annotation { "Feature Type Name" : "Feature", "Feature Type Description" : "" }
export const myFeature = defineFeature(function(context is Context, id is Id, definition is map)
    precondition{}
    {
        {
            var Q0;
            Q0=qCreatedBy(makeId("Top.planeOp"),FACE);
            var sketch = newSketch(context, id + "F0", { "sketchPlane" : qUnion([Q0])});
            skLineSegment(sketch, "E0.bottom", {"start": v(-26.5, -42.5) * mm, "end": v(26.5, -42.5) * mm});
            skLineSegment(sketch, "E0.top", {"start": v(-23.72, 42.5) * mm, "end": v(-23.1, 42.5) * mm});
            skLineSegment(sketch, "E0.left", {"start": v(-26.5, -42.5) * mm, "end": v(-26.5, 0) * mm});
            skLineSegment(sketch, "E0.right", {"start": v(26.5, -42.5) * mm, "end": v(26.5, 0) * mm});
            skPoint(sketch, "E0.middle", {"position": v(0, 0) * mm});
            skLineSegment(sketch, "E1.top", {"start": v(-0.6, 85) * mm, "end": v(0.6, 85) * mm});
            skLineSegment(sketch, "E1.left", {"start": v(-0.6, 0) * mm, "end": v(-0.6, 41.9) * mm});
            skLineSegment(sketch, "E1.right", {"start": v(0.6, 0) * mm, "end": v(0.6, 41.9) * mm});
            skPoint(sketch, "E1.middle", {"position": v(0, 42.5) * mm});
            skLineSegment(sketch, "E2.1.0.0", {"start": v(3.6, 0) * mm, "end": v(3.6, 41.9) * mm});
            skLineSegment(sketch, "E2.1.0.1", {"start": v(2.4, 0) * mm, "end": v(2.4, 41.9) * mm});
            skLineSegment(sketch, "E2.2.0.0", {"start": v(6.6, 0) * mm, "end": v(6.6, 41.9) * mm});
            skLineSegment(sketch, "E2.2.0.1", {"start": v(5.4, 0) * mm, "end": v(5.4, 41.9) * mm});
            skLineSegment(sketch, "E2.3.0.0", {"start": v(9.6, 0) * mm, "end": v(9.6, 41.9) * mm});
            skLineSegment(sketch, "E2.3.0.1", {"start": v(8.4, 0) * mm, "end": v(8.4, 41.9) * mm});
            skLineSegment(sketch, "E2.4.0.0", {"start": v(12.6, 0) * mm, "end": v(12.6, 41.92) * mm});
            skLineSegment(sketch, "E2.4.0.1", {"start": v(11.4, 0) * mm, "end": v(11.4, 41.9) * mm});
            skLineSegment(sketch, "E2.5.0.0", {"start": v(15.6, 0) * mm, "end": v(15.6, 41.9) * mm});
            skLineSegment(sketch, "E2.5.0.1", {"start": v(14.4, 0) * mm, "end": v(14.4, 41.9) * mm});
            skLineSegment(sketch, "E2.6.0.0", {"start": v(18.6, 0) * mm, "end": v(18.6, 41.9) * mm});
            skLineSegment(sketch, "E2.6.0.1", {"start": v(17.4, 0) * mm, "end": v(17.4, 41.9) * mm});
            skLineSegment(sketch, "E2.7.0.0", {"start": v(21.6, 0) * mm, "end": v(21.6, 41.9) * mm});
            skLineSegment(sketch, "E2.7.0.1", {"start": v(20.4, 0) * mm, "end": v(20.4, 41.9) * mm});
            skLineSegment(sketch, "E2.direction1", {"start": v(0.6, 0) * mm, "end": v(2.4, 0) * mm, "construction": true});
            skLineSegment(sketch, "E3", {"start": v(21.6, 42.5) * mm, "end": v(20.4, 42.5) * mm});
            skPoint(sketch, "E4.orphan", {"position": v(3.6, 85) * mm});
            skPoint(sketch, "E5.orphan", {"position": v(2.4, 85) * mm});
            skPoint(sketch, "E6.orphan", {"position": v(5.4, 85) * mm});
            skPoint(sketch, "E7.orphan", {"position": v(6.6, 85) * mm});
            skPoint(sketch, "E8.orphan", {"position": v(8.4, 85) * mm});
            skPoint(sketch, "E9.orphan", {"position": v(9.6, 85) * mm});
            skPoint(sketch, "E10.orphan", {"position": v(11.4, 85) * mm});
            skPoint(sketch, "E11.orphan", {"position": v(12.6, 85) * mm});
            skPoint(sketch, "E12.orphan", {"position": v(15.6, 85) * mm});
            skPoint(sketch, "E13.orphan", {"position": v(14.4, 85) * mm});
            skPoint(sketch, "E14.orphan", {"position": v(18.6, 85) * mm});
            skPoint(sketch, "E15.orphan", {"position": v(17.4, 85) * mm});
            skPoint(sketch, "E16.orphan", {"position": v(20.4, 85) * mm});
            skPoint(sketch, "E17.orphan", {"position": v(21.6, 85) * mm});
            skLineSegment(sketch, "E18.trimOffspring", {"start": v(2.4, 0) * mm, "end": v(0.6, 0) * mm});
            skLineSegment(sketch, "E19.trimOffspring", {"start": v(18.6, 42.5) * mm, "end": v(17.4, 42.5) * mm});
            skLineSegment(sketch, "E20.trimOffspring", {"start": v(15.6, 42.5) * mm, "end": v(14.4, 42.5) * mm});
            skLineSegment(sketch, "E21.trimOffspring", {"start": v(20.4, 42.5) * mm, "end": v(21.6, 42.5) * mm});
            skLineSegment(sketch, "E22.trimOffspring", {"start": v(17.4, 42.5) * mm, "end": v(18.6, 42.5) * mm});
            skLineSegment(sketch, "E23.trimOffspring", {"start": v(12.6, 42.5) * mm, "end": v(11.4, 42.5) * mm});
            skLineSegment(sketch, "E24.trimOffspring", {"start": v(11.4, 42.5) * mm, "end": v(12.6, 42.5) * mm});
            skLineSegment(sketch, "E25.trimOffspring", {"start": v(14.4, 42.5) * mm, "end": v(15.6, 42.5) * mm});
            skLineSegment(sketch, "E26.trimOffspring", {"start": v(6.6, 42.5) * mm, "end": v(5.4, 42.5) * mm});
            skLineSegment(sketch, "E27.trimOffspring", {"start": v(8.4, 42.5) * mm, "end": v(9.6, 42.5) * mm});
            skLineSegment(sketch, "E28.trimOffspring", {"start": v(3.6, 42.5) * mm, "end": v(2.4, 42.5) * mm});
            skLineSegment(sketch, "E29.trimOffspring", {"start": v(5.4, 42.5) * mm, "end": v(6.6, 42.5) * mm});
            skLineSegment(sketch, "E30.trimOffspring", {"start": v(0.6, 42.5) * mm, "end": v(-0.6, 42.5) * mm});
            skLineSegment(sketch, "E31.trimOffspring", {"start": v(2.4, 42.5) * mm, "end": v(3.6, 42.5) * mm});
            skLineSegment(sketch, "E32.MirrorCS", {"start": v(-21.6, 0) * mm, "end": v(-21.6, 41.9) * mm});
            skLineSegment(sketch, "E33.MirrorCS", {"start": v(-20.4, 0) * mm, "end": v(-20.4, 41.9) * mm});
            skLineSegment(sketch, "E34.MirrorCS", {"start": v(-18.6, 0) * mm, "end": v(-18.6, 41.9) * mm});
            skLineSegment(sketch, "E35.MirrorCS", {"start": v(-17.4, 0) * mm, "end": v(-17.4, 41.9) * mm});
            skLineSegment(sketch, "E36.MirrorCS", {"start": v(-15.6, 0) * mm, "end": v(-15.6, 41.9) * mm});
            skLineSegment(sketch, "E37.MirrorCS", {"start": v(-14.4, 0) * mm, "end": v(-14.4, 41.9) * mm});
            skLineSegment(sketch, "E38.MirrorCS", {"start": v(-12.6, 0) * mm, "end": v(-12.6, 41.9) * mm});
            skLineSegment(sketch, "E39.MirrorCS", {"start": v(-11.4, 0) * mm, "end": v(-11.4, 41.9) * mm});
            skLineSegment(sketch, "E40.MirrorCS", {"start": v(-9.6, 0) * mm, "end": v(-9.6, 41.9) * mm});
            skLineSegment(sketch, "E41.MirrorCS", {"start": v(-8.4, 0) * mm, "end": v(-8.4, 41.9) * mm});
            skLineSegment(sketch, "E42.MirrorCS", {"start": v(-6.6, 0) * mm, "end": v(-6.6, 41.9) * mm});
            skLineSegment(sketch, "E43.MirrorCS", {"start": v(-5.4, 0) * mm, "end": v(-5.4, 41.9) * mm});
            skLineSegment(sketch, "E44.MirrorCS", {"start": v(-3.6, 0) * mm, "end": v(-3.6, 41.9) * mm});
            skLineSegment(sketch, "E45.MirrorCS", {"start": v(-2.4, 0) * mm, "end": v(-2.4, 41.9) * mm});
            skLineSegment(sketch, "E46.trimOffspring", {"start": v(-18.6, 42.5) * mm, "end": v(-17.4, 42.5) * mm});
            skLineSegment(sketch, "E47.trimOffspring", {"start": v(-15.6, 42.5) * mm, "end": v(-14.4, 42.5) * mm});
            skLineSegment(sketch, "E48.trimOffspring", {"start": v(-20.4, 42.5) * mm, "end": v(-21.6, 42.5) * mm});
            skLineSegment(sketch, "E49.trimOffspring", {"start": v(-17.4, 42.5) * mm, "end": v(-18.6, 42.5) * mm});
            skLineSegment(sketch, "E50.trimOffspring", {"start": v(-12.6, 42.5) * mm, "end": v(-11.4, 42.5) * mm});
            skLineSegment(sketch, "E51.trimOffspring", {"start": v(-14.4, 42.5) * mm, "end": v(-15.6, 42.5) * mm});
            skLineSegment(sketch, "E52.trimOffspring", {"start": v(-9.6, 42.5) * mm, "end": v(-8.4, 42.5) * mm});
            skLineSegment(sketch, "E53.trimOffspring", {"start": v(-11.4, 42.5) * mm, "end": v(-12.6, 42.5) * mm});
            skLineSegment(sketch, "E54.trimOffspring", {"start": v(-6.6, 42.5) * mm, "end": v(-5.4, 42.5) * mm});
            skLineSegment(sketch, "E55.trimOffspring", {"start": v(-3.6, 42.5) * mm, "end": v(-2.4, 42.5) * mm});
            skLineSegment(sketch, "E56.trimOffspring", {"start": v(-8.4, 42.5) * mm, "end": v(-9.6, 42.5) * mm});
            skLineSegment(sketch, "E57.trimOffspring", {"start": v(-6, 42.5) * mm, "end": v(-6.6, 42.5) * mm});
            skLineSegment(sketch, "E58.trimOffspring", {"start": v(-0.6, 42.5) * mm, "end": v(0.6, 42.5) * mm});
            skLineSegment(sketch, "E59.trimOffspring", {"start": v(-2.4, 42.5) * mm, "end": v(-3.6, 42.5) * mm});
            skLineSegment(sketch, "E60", {"start": v(-24.33, 41.93) * mm, "end": v(-26.5, 0) * mm});
            skLineSegment(sketch, "E61", {"start": v(-23.1, 41.9) * mm, "end": v(-23.1, 0) * mm});
            skLineSegment(sketch, "E62.trimOffspring", {"start": v(-21.6, 42.5) * mm, "end": v(-20.4, 42.5) * mm});
            skLineSegment(sketch, "E63.trimOffspring", {"start": v(-23.1, 42.5) * mm, "end": v(-24.3, 42.5) * mm});
            skPoint(sketch, "E64.orphan", {"position": v(-26.5, 42.5) * mm});
            skLineSegment(sketch, "E65", {"start": v(23.1, 41.88) * mm, "end": v(23.1, 0) * mm});
            skPoint(sketch, "E65.endSnap0", {"position": v(26.5, 0) * mm});
            skLineSegment(sketch, "E66", {"start": v(24.33, 41.95) * mm, "end": v(26.5, 0) * mm});
            skPoint(sketch, "E67.orphan", {"position": v(26.5, 42.5) * mm});
            skLineSegment(sketch, "E68.trimOffspring", {"start": v(23.1, 42.5) * mm, "end": v(24.3, 42.5) * mm});
            skLineSegment(sketch, "E69", {"start": v(-23.1, 0) * mm, "end": v(-21.6, 0) * mm});
            skLineSegment(sketch, "E70.trimOffspring", {"start": v(-20.4, 0) * mm, "end": v(-18.6, 0) * mm});
            skLineSegment(sketch, "E71.trimOffspring", {"start": v(-17.4, 0) * mm, "end": v(-15.6, 0) * mm});
            skLineSegment(sketch, "E72.trimOffspring", {"start": v(-14.4, 0) * mm, "end": v(-12.6, 0) * mm});
            skLineSegment(sketch, "E73.trimOffspring", {"start": v(-11.4, 0) * mm, "end": v(-9.6, 0) * mm});
            skLineSegment(sketch, "E74.trimOffspring", {"start": v(-8.4, 0) * mm, "end": v(-6.6, 0) * mm});
            skLineSegment(sketch, "E75.trimOffspring", {"start": v(-5.4, 0) * mm, "end": v(-3.6, 0) * mm});
            skLineSegment(sketch, "E76.trimOffspring", {"start": v(-2.4, 0) * mm, "end": v(-0.6, 0) * mm});
            skLineSegment(sketch, "E77.trimOffspring", {"start": v(0.6, 0) * mm, "end": v(2.4, 0) * mm});
            skLineSegment(sketch, "E78.trimOffspring", {"start": v(3.6, 0) * mm, "end": v(5.4, 0) * mm});
            skLineSegment(sketch, "E79.trimOffspring", {"start": v(6.6, 0) * mm, "end": v(8.4, 0) * mm});
            skLineSegment(sketch, "E80.trimOffspring", {"start": v(9.6, 0) * mm, "end": v(11.4, 0) * mm});
            skLineSegment(sketch, "E81.trimOffspring", {"start": v(12.6, 0) * mm, "end": v(14.4, 0) * mm});
            skLineSegment(sketch, "E82.trimOffspring", {"start": v(15.6, 0) * mm, "end": v(17.4, 0) * mm});
            skLineSegment(sketch, "E83.trimOffspring", {"start": v(18.6, 0) * mm, "end": v(20.4, 0) * mm});
            skLineSegment(sketch, "E84.trimOffspring", {"start": v(21.6, 0) * mm, "end": v(23.1, 0) * mm});
            skArc(sketch, "E85", {"start": v(-20.4, 41.9) * mm, "mid": v(-21, 42.5) * mm, "end": v(-21.6, 41.9) * mm});
            skArc(sketch, "E86", {"start": v(-17.4, 41.9) * mm, "mid": v(-18, 42.5) * mm, "end": v(-18.6, 41.9) * mm});
            skArc(sketch, "E87", {"start": v(-14.4, 41.9) * mm, "mid": v(-15, 42.5) * mm, "end": v(-15.6, 41.9) * mm});
            skArc(sketch, "E88", {"start": v(-11.4, 41.9) * mm, "mid": v(-12, 42.5) * mm, "end": v(-12.6, 41.9) * mm});
            skArc(sketch, "E89", {"start": v(-5.4, 41.9) * mm, "mid": v(-6, 42.5) * mm, "end": v(-6.6, 41.9) * mm});
            skArc(sketch, "E90", {"start": v(-2.4, 41.9) * mm, "mid": v(-3, 42.5) * mm, "end": v(-3.6, 41.9) * mm});
            skArc(sketch, "E91", {"start": v(0.6, 41.9) * mm, "mid": v(0, 42.5) * mm, "end": v(-0.6, 41.9) * mm});
            skArc(sketch, "E92", {"start": v(-8.4, 41.9) * mm, "mid": v(-9, 42.5) * mm, "end": v(-9.6, 41.9) * mm});
            skArc(sketch, "E93", {"start": v(3.6, 41.9) * mm, "mid": v(3, 42.5) * mm, "end": v(2.4, 41.9) * mm});
            skArc(sketch, "E94", {"start": v(6.6, 41.9) * mm, "mid": v(6, 42.5) * mm, "end": v(5.4, 41.9) * mm});
            skArc(sketch, "E95", {"start": v(9.6, 41.9) * mm, "mid": v(9, 42.5) * mm, "end": v(8.4, 41.9) * mm});
            skArc(sketch, "E96", {"start": v(12.6, 41.88) * mm, "mid": v(12, 42.5) * mm, "end": v(11.4, 41.9) * mm});
            skArc(sketch, "E97", {"start": v(15.6, 41.9) * mm, "mid": v(15, 42.5) * mm, "end": v(14.4, 41.9) * mm});
            skArc(sketch, "E98", {"start": v(18.6, 41.9) * mm, "mid": v(18, 42.5) * mm, "end": v(17.4, 41.9) * mm});
            skArc(sketch, "E99", {"start": v(24.33, 41.88) * mm, "mid": v(23.72, 42.5) * mm, "end": v(23.1, 41.88) * mm});
            skArc(sketch, "E100", {"start": v(21.6, 41.9) * mm, "mid": v(21, 42.5) * mm, "end": v(20.4, 41.9) * mm});
            skArc(sketch, "E101", {"start": v(-23.1, 41.9) * mm, "mid": v(-23.72, 42.5) * mm, "end": v(-24.33, 41.9) * mm});
            skSolve(sketch);
        }
        {
            var Q0;
            Q0 = qSketchRegion(id + "F0", true);
            extrude(context, id + "F1", {"entities" : qUnion([Q0]), "depth" : 1.5 * mm, "offsetDistance" : 25 * mm});
        }
        {
            var Q0;
            Q0=makeQuery(id+"F1.opExtrude","CAP_FACE",FACE,{"disambiguationData":[OSD([sQuery(id+"F0.wireOp",EDGE,"E0.bottom"),sQuery(id+"F0.wireOp",EDGE,"E0.left"),sQuery(id+"F0.wireOp",EDGE,"E0.right"),sQuery(id+"F0.wireOp",EDGE,"E1.left"),sQuery(id+"F0.wireOp",EDGE,"E1.right"),sQuery(id+"F0.wireOp",EDGE,"E2.1.0.0"),sQuery(id+"F0.wireOp",EDGE,"E2.1.0.1"),sQuery(id+"F0.wireOp",EDGE,"E2.2.0.0"),sQuery(id+"F0.wireOp",EDGE,"E2.2.0.1"),sQuery(id+"F0.wireOp",EDGE,"E2.3.0.0"),sQuery(id+"F0.wireOp",EDGE,"E2.3.0.1"),sQuery(id+"F0.wireOp",EDGE,"E2.4.0.0"),sQuery(id+"F0.wireOp",EDGE,"E2.4.0.1"),sQuery(id+"F0.wireOp",EDGE,"E2.5.0.0"),sQuery(id+"F0.wireOp",EDGE,"E2.5.0.1"),sQuery(id+"F0.wireOp",EDGE,"E2.6.0.0"),sQuery(id+"F0.wireOp",EDGE,"E2.6.0.1"),sQuery(id+"F0.wireOp",EDGE,"E2.7.0.0"),sQuery(id+"F0.wireOp",EDGE,"E2.7.0.1"),sQuery(id+"F0.wireOp",EDGE,"E32.MirrorCS"),sQuery(id+"F0.wireOp",EDGE,"E33.MirrorCS"),sQuery(id+"F0.wireOp",EDGE,"E34.MirrorCS"),sQuery(id+"F0.wireOp",EDGE,"E35.MirrorCS"),sQuery(id+"F0.wireOp",EDGE,"E36.MirrorCS"),sQuery(id+"F0.wireOp",EDGE,"E37.MirrorCS"),sQuery(id+"F0.wireOp",EDGE,"E38.MirrorCS"),sQuery(id+"F0.wireOp",EDGE,"E39.MirrorCS"),sQuery(id+"F0.wireOp",EDGE,"E40.MirrorCS"),sQuery(id+"F0.wireOp",EDGE,"E41.MirrorCS"),sQuery(id+"F0.wireOp",EDGE,"E42.MirrorCS"),sQuery(id+"F0.wireOp",EDGE,"E43.MirrorCS"),sQuery(id+"F0.wireOp",EDGE,"E44.MirrorCS"),sQuery(id+"F0.wireOp",EDGE,"E45.MirrorCS"),sQuery(id+"F0.wireOp",EDGE,"E60"),sQuery(id+"F0.wireOp",EDGE,"E61"),sQuery(id+"F0.wireOp",EDGE,"E65"),sQuery(id+"F0.wireOp",EDGE,"E66"),sQuery(id+"F0.wireOp",EDGE,"E69"),sQuery(id+"F0.wireOp",EDGE,"E70.trimOffspring"),sQuery(id+"F0.wireOp",EDGE,"E71.trimOffspring"),sQuery(id+"F0.wireOp",EDGE,"E72.trimOffspring"),sQuery(id+"F0.wireOp",EDGE,"E73.trimOffspring"),sQuery(id+"F0.wireOp",EDGE,"E74.trimOffspring"),sQuery(id+"F0.wireOp",EDGE,"E75.trimOffspring"),sQuery(id+"F0.wireOp",EDGE,"E76.trimOffspring"),sQuery(id+"F0.wireOp",EDGE,"E77.trimOffspring"),sQuery(id+"F0.wireOp",EDGE,"E78.trimOffspring"),sQuery(id+"F0.wireOp",EDGE,"E79.trimOffspring"),sQuery(id+"F0.wireOp",EDGE,"E80.trimOffspring"),sQuery(id+"F0.wireOp",EDGE,"E81.trimOffspring"),sQuery(id+"F0.wireOp",EDGE,"E82.trimOffspring"),sQuery(id+"F0.wireOp",EDGE,"E83.trimOffspring"),sQuery(id+"F0.wireOp",EDGE,"E84.trimOffspring"),sQuery(id+"F0.wireOp",EDGE,"E85"),sQuery(id+"F0.wireOp",EDGE,"E86"),sQuery(id+"F0.wireOp",EDGE,"E87"),sQuery(id+"F0.wireOp",EDGE,"E88"),sQuery(id+"F0.wireOp",EDGE,"E89"),sQuery(id+"F0.wireOp",EDGE,"E90"),sQuery(id+"F0.wireOp",EDGE,"E91"),sQuery(id+"F0.wireOp",EDGE,"E92"),sQuery(id+"F0.wireOp",EDGE,"E93"),sQuery(id+"F0.wireOp",EDGE,"E94"),sQuery(id+"F0.wireOp",EDGE,"E95"),sQuery(id+"F0.wireOp",EDGE,"E96"),sQuery(id+"F0.wireOp",EDGE,"E97"),sQuery(id+"F0.wireOp",EDGE,"E98"),sQuery(id+"F0.wireOp",EDGE,"E99"),sQuery(id+"F0.wireOp",EDGE,"E100"),sQuery(id+"F0.wireOp",EDGE,"E101")])],"isStart":false});
            var sketch = newSketch(context, id + "F2", { "sketchPlane" : qUnion([Q0])});
            skLineSegment(sketch, "E102", {"start": v(-23.1, 6.5) * mm, "end": v(-23.1, 0) * mm});
            skLineSegment(sketch, "E103", {"start": v(-23.1, 0) * mm, "end": v(23.1, 0) * mm});
            skLineSegment(sketch, "E104", {"start": v(23.1, 0) * mm, "end": v(23.1, 6.5) * mm});
            skArc(sketch, "E105", {"start": v(-23.1, 6.5) * mm, "mid": v(0, 1.57) * mm, "end": v(23.1, 6.5) * mm});
            skSolve(sketch);
        }
        {
            var Q0;
            Q0 = qSketchRegion(id + "F2", true);
            extrude(context, id + "F3", {"entities" : qUnion([Q0]), "operationType" : NewBodyOperationType.ADD, "oppositeDirection" : true, "depth" : 1.5 * mm, "offsetDistance" : 25 * mm});
        }
        {
            var Q0;
            Q0=makeQuery(id+"F3.boolean.opBoolean","MERGE",FACE,{"derivedFrom":[makeQuery(id+"F1.opExtrude","CAP_FACE",FACE,{"disambiguationData":[OSD([sQuery(id+"F0.wireOp",EDGE,"E0.bottom"),sQuery(id+"F0.wireOp",EDGE,"E0.left"),sQuery(id+"F0.wireOp",EDGE,"E0.right"),sQuery(id+"F0.wireOp",EDGE,"E1.left"),sQuery(id+"F0.wireOp",EDGE,"E1.right"),sQuery(id+"F0.wireOp",EDGE,"E2.1.0.0"),sQuery(id+"F0.wireOp",EDGE,"E2.1.0.1"),sQuery(id+"F0.wireOp",EDGE,"E2.2.0.0"),sQuery(id+"F0.wireOp",EDGE,"E2.2.0.1"),sQuery(id+"F0.wireOp",EDGE,"E2.3.0.0"),sQuery(id+"F0.wireOp",EDGE,"E2.3.0.1"),sQuery(id+"F0.wireOp",EDGE,"E2.4.0.0"),sQuery(id+"F0.wireOp",EDGE,"E2.4.0.1"),sQuery(id+"F0.wireOp",EDGE,"E2.5.0.0"),sQuery(id+"F0.wireOp",EDGE,"E2.5.0.1"),sQuery(id+"F0.wireOp",EDGE,"E2.6.0.0"),sQuery(id+"F0.wireOp",EDGE,"E2.6.0.1"),sQuery(id+"F0.wireOp",EDGE,"E2.7.0.0"),sQuery(id+"F0.wireOp",EDGE,"E2.7.0.1"),sQuery(id+"F0.wireOp",EDGE,"E32.MirrorCS"),sQuery(id+"F0.wireOp",EDGE,"E33.MirrorCS"),sQuery(id+"F0.wireOp",EDGE,"E34.MirrorCS"),sQuery(id+"F0.wireOp",EDGE,"E35.MirrorCS"),sQuery(id+"F0.wireOp",EDGE,"E36.MirrorCS"),sQuery(id+"F0.wireOp",EDGE,"E37.MirrorCS"),sQuery(id+"F0.wireOp",EDGE,"E38.MirrorCS"),sQuery(id+"F0.wireOp",EDGE,"E39.MirrorCS"),sQuery(id+"F0.wireOp",EDGE,"E40.MirrorCS"),sQuery(id+"F0.wireOp",EDGE,"E41.MirrorCS"),sQuery(id+"F0.wireOp",EDGE,"E42.MirrorCS"),sQuery(id+"F0.wireOp",EDGE,"E43.MirrorCS"),sQuery(id+"F0.wireOp",EDGE,"E44.MirrorCS"),sQuery(id+"F0.wireOp",EDGE,"E45.MirrorCS"),sQuery(id+"F0.wireOp",EDGE,"E60"),sQuery(id+"F0.wireOp",EDGE,"E61"),sQuery(id+"F0.wireOp",EDGE,"E65"),sQuery(id+"F0.wireOp",EDGE,"E66"),sQuery(id+"F0.wireOp",EDGE,"E69"),sQuery(id+"F0.wireOp",EDGE,"E70.trimOffspring"),sQuery(id+"F0.wireOp",EDGE,"E71.trimOffspring"),sQuery(id+"F0.wireOp",EDGE,"E72.trimOffspring"),sQuery(id+"F0.wireOp",EDGE,"E73.trimOffspring"),sQuery(id+"F0.wireOp",EDGE,"E74.trimOffspring"),sQuery(id+"F0.wireOp",EDGE,"E75.trimOffspring"),sQuery(id+"F0.wireOp",EDGE,"E76.trimOffspring"),sQuery(id+"F0.wireOp",EDGE,"E77.trimOffspring"),sQuery(id+"F0.wireOp",EDGE,"E78.trimOffspring"),sQuery(id+"F0.wireOp",EDGE,"E79.trimOffspring"),sQuery(id+"F0.wireOp",EDGE,"E80.trimOffspring"),sQuery(id+"F0.wireOp",EDGE,"E81.trimOffspring"),sQuery(id+"F0.wireOp",EDGE,"E82.trimOffspring"),sQuery(id+"F0.wireOp",EDGE,"E83.trimOffspring"),sQuery(id+"F0.wireOp",EDGE,"E84.trimOffspring"),sQuery(id+"F0.wireOp",EDGE,"E85"),sQuery(id+"F0.wireOp",EDGE,"E86"),sQuery(id+"F0.wireOp",EDGE,"E87"),sQuery(id+"F0.wireOp",EDGE,"E88"),sQuery(id+"F0.wireOp",EDGE,"E89"),sQuery(id+"F0.wireOp",EDGE,"E90"),sQuery(id+"F0.wireOp",EDGE,"E91"),sQuery(id+"F0.wireOp",EDGE,"E92"),sQuery(id+"F0.wireOp",EDGE,"E93"),sQuery(id+"F0.wireOp",EDGE,"E94"),sQuery(id+"F0.wireOp",EDGE,"E95"),sQuery(id+"F0.wireOp",EDGE,"E96"),sQuery(id+"F0.wireOp",EDGE,"E97"),sQuery(id+"F0.wireOp",EDGE,"E98"),sQuery(id+"F0.wireOp",EDGE,"E99"),sQuery(id+"F0.wireOp",EDGE,"E100"),sQuery(id+"F0.wireOp",EDGE,"E101")])],"isStart":true}),makeQuery(id+"F3.opExtrude","CAP_FACE",FACE,{"disambiguationData":[OSD([sQuery(id+"F2.wireOp",EDGE,"E102"),sQuery(id+"F2.wireOp",EDGE,"E103"),sQuery(id+"F2.wireOp",EDGE,"E104"),sQuery(id+"F2.wireOp",EDGE,"E105")])],"isStart":false})]});
            var sketch = newSketch(context, id + "F4", { "sketchPlane" : qUnion([Q0])});
            skText(sketch, "E106", { "text": "Sanso Brother\'s\nCustom Pet Toys", "fontName": "Tinos-Bold.ttf"});
            skText(sketch, "E107", { "text": "Email: \<email>", "fontName": "OpenSans-Bold.ttf"});
            skText(sketch, "E108", { "text": "Phone: 303-601-8332", "fontName": "Arimo-Bold.ttf"});
            skText(sketch, "E109", { "text": "Daniel Sanso", "fontName": "Tinos-BoldItalic.ttf"});
            skText(sketch, "E110", { "text": "CEO", "fontName": "OpenSans-BoldItalic.ttf"});
            const initialGuessF4  = {"E106": [-0.025, 0.03358, 1, 0, 0.00492], "E107": [-0.0225, 0.01272, 1, 0, 0.00278], "E108": [-0.0225, 0.00096, 1, 0, 0.00327], "E109": [-0.0205, 0.01858, 1, 0, 0.00388], "E110": [0.0105, 0.0177, 1, 0, 0.00188]};
            skSetInitialGuess(sketch, initialGuessF4);
            skSolve(sketch);
        }
        {
            var Q0;
            Q0 = qSketchRegion(id + "F4", true);
            extrude(context, id + "F5", {"entities" : qUnion([Q0]), "operationType" : NewBodyOperationType.REMOVE, "oppositeDirection" : true, "depth" : .5 * mm, "offsetDistance" : 25 * mm});
        }
    });